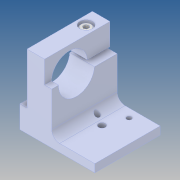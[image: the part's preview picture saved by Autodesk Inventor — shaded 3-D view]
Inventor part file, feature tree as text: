
AUTODESK INVENTOR PART (.ipt)
format: ipt  version: 2019 (Build 230136000, 136)  size: 246,784 bytes
history: native  units: mm
features: projected_geometry x5, extrude x4, sketch x4, other x2
ambient origin geometry x8: Origin, YZ Plane, XZ Plane, XY Plane, X Axis, Y Axis, Z Axis, Center Point
bodies: Solid1 (feature_tree), Solid3 (feature_tree)
feature tree (15):
  extrude  "Extrusion1"  Depth=10.0mm TaperAngle=0.0deg
  extrude  "Extrusion2"  Depth=4.5mm TaperAngle=0.0deg
  extrude  "Extrusion3"  Depth=4.5mm TaperAngle=0.0deg
  extrude  "Extrusion4"  [1 undecoded]
  sketch  "Sketch1"  dims[d0=10.0mm d1=0.0mm d2=10.0mm d3=0.0mm]
  projected_geometry  "Projected Loop1"
  sketch  "Sketch2"  dims[d4=14.0mm d5=4.5mm d6=0.0mm]
  projected_geometry  "Projected Loop2"
  projected_geometry  "Projected Loop3"
  sketch  "Sketch3"  dims[d7=32.0mm d8=4.5mm d9=0.0mm]
  projected_geometry  "Projected Loop4"
  sketch  "Sketch4"
  projected_geometry  "Projected Loop5"
  parser-record x1  (decoder bookkeeping rows leaked as tree rows — omitted from the tree; the rows remain in map.json)
  other  "NONE:2"
note: 1 required parameter value undecoded (feature->parameter linkage not recoverable at this tier; creation-order binding heuristic only, values carry confidence <= 0.55)
